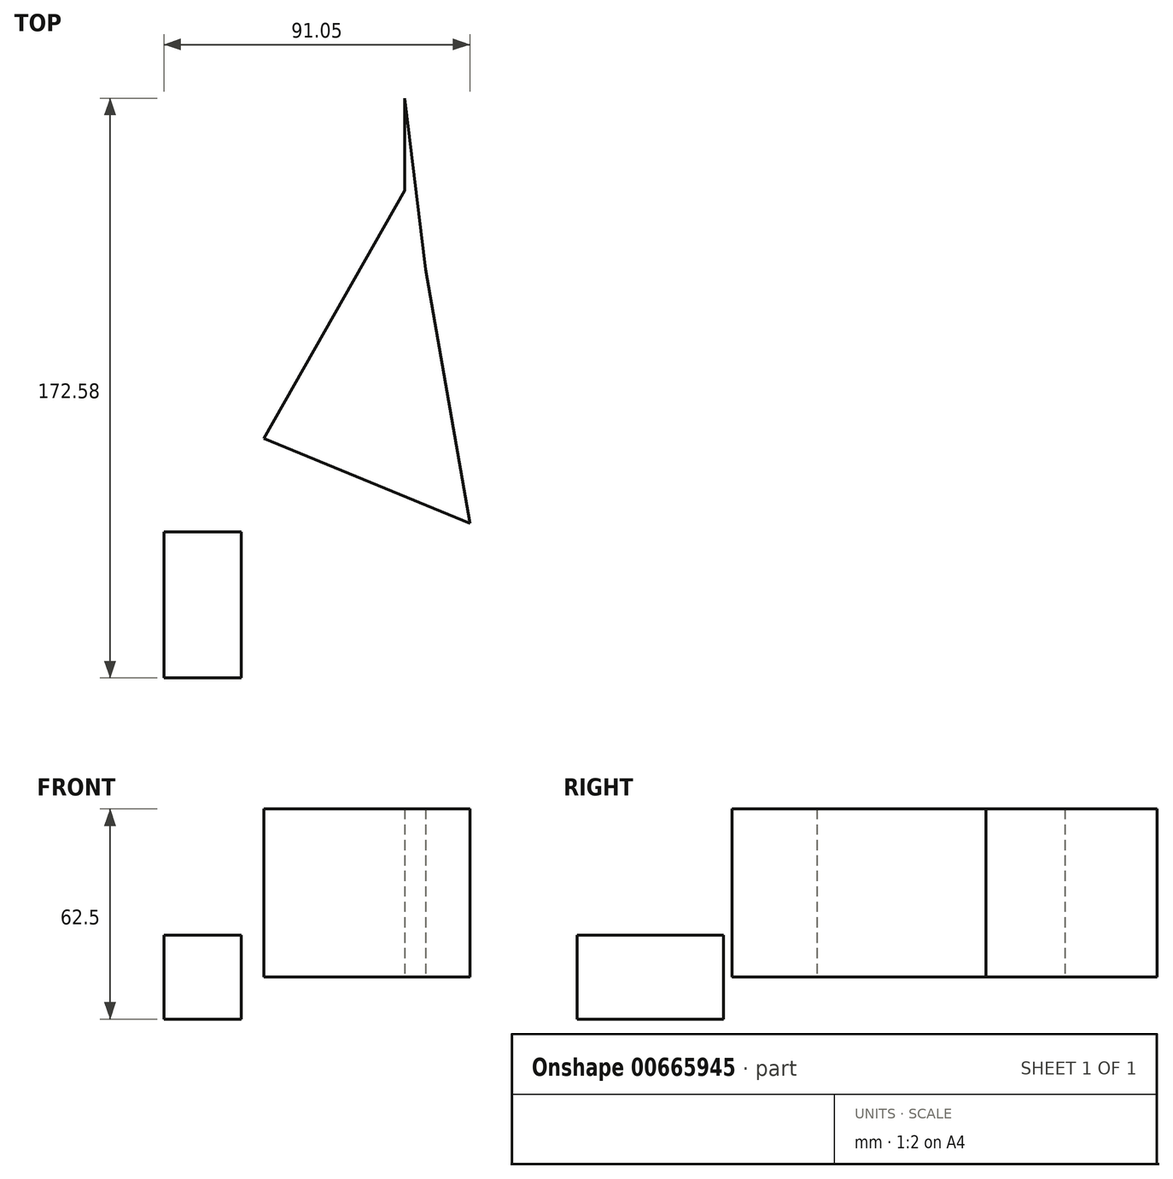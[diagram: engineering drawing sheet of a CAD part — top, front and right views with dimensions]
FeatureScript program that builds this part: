
annotation { "Feature Type Name" : "Feature", "Feature Type Description" : "" }
export const myFeature = defineFeature(function(context is Context, id is Id, definition is map)
    precondition{}
    {
        {
            var Q0;
            Q0=qCreatedBy(makeId("Top.planeOp"),FACE);
            var sketch = newSketch(context, id + "F0", { "sketchPlane" : qUnion([Q0])});
            skLineSegment(sketch, "E0.bottom", {"start": v(-36.93, 25.92) * mm, "end": v(-59.91, 25.92) * mm});
            skLineSegment(sketch, "E0.top", {"start": v(-36.93, 69.44) * mm, "end": v(-59.91, 69.44) * mm});
            skLineSegment(sketch, "E0.left", {"start": v(-36.93, 25.92) * mm, "end": v(-36.93, 69.44) * mm});
            skLineSegment(sketch, "E0.right", {"start": v(-59.91, 25.92) * mm, "end": v(-59.91, 69.44) * mm});
            skSolve(sketch);
        }
        {
            var Q0;
            Q0 = qSketchRegion(id + "F0", true);
            extrude(context, id + "F1", {"entities" : qUnion([Q0]), "endBound" : BoundingType.SYMMETRIC, "depth" : 25 * mm, "offsetDistance" : 25.4 * mm});
        }
        {
            var Q0;
            Q0=qCreatedBy(makeId("Top.planeOp"),FACE);
            var sketch = newSketch(context, id + "F2", { "sketchPlane" : qUnion([Q0])});
            skLineSegment(sketch, "E1", {"start": v(18.01, 147.52) * mm, "end": v(31.14, 72) * mm});
            skLineSegment(sketch, "E2", {"start": v(31.14, 72) * mm, "end": v(-30.08, 97.18) * mm});
            skLineSegment(sketch, "E3", {"start": v(-30.08, 97.18) * mm, "end": v(11.82, 170.97) * mm});
            skLineSegment(sketch, "E4", {"start": v(11.82, 170.97) * mm, "end": v(11.82, 198.5) * mm});
            skLineSegment(sketch, "E5", {"start": v(11.82, 198.5) * mm, "end": v(18.01, 147.52) * mm});
            skSolve(sketch);
        }
        {
            var Q0;
            Q0=makeQuery(id+"F2.imprint","IMPRINT",FACE,{"disambiguationData":[TD([[makeQuery(id+"F2.imprint","IMPRINT",EDGE,{"derivedFrom":sQuery(id+"F2.wireOp",EDGE,"E1")}),-1.0]])]});
            extrude(context, id + "F3", {"entities" : qUnion([Q0]), "depth" : 50 * mm, "offsetDistance" : 25 * mm});
        }
    });
